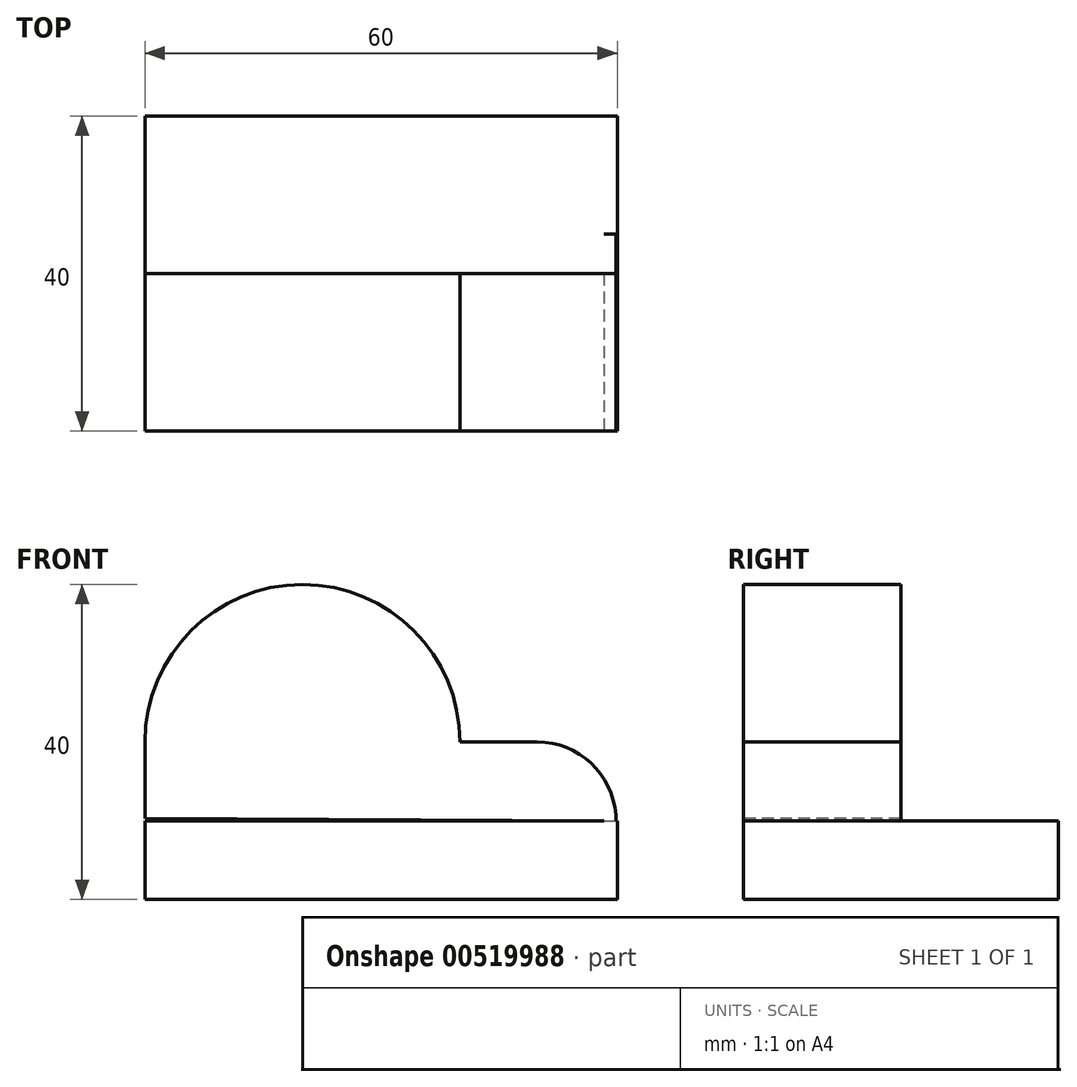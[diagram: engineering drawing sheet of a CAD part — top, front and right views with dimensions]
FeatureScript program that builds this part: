
annotation { "Feature Type Name" : "Feature", "Feature Type Description" : "" }
export const myFeature = defineFeature(function(context is Context, id is Id, definition is map)
    precondition{}
    {
        {
            var Q0;
            Q0=qCreatedBy(makeId("Top.planeOp"),FACE);
            var sketch = newSketch(context, id + "F0", { "sketchPlane" : qUnion([Q0])});
            skLineSegment(sketch, "E0.bottom", {"start": v(0, 0) * mm, "end": v(60, 0) * mm});
            skLineSegment(sketch, "E0.top", {"start": v(0, 40) * mm, "end": v(60, 40) * mm});
            skLineSegment(sketch, "E0.left", {"start": v(0, 0) * mm, "end": v(0, 40) * mm});
            skLineSegment(sketch, "E0.right", {"start": v(60, 0) * mm, "end": v(60, 40) * mm});
            skSolve(sketch);
        }
        {
            var Q0;
            Q0=makeQuery(id+"F0.imprint","IMPRINT",FACE,{"disambiguationData":[TD([[makeQuery(id+"F0.imprint","IMPRINT",EDGE,{"derivedFrom":sQuery(id+"F0.wireOp",EDGE,"E0.bottom")}),1.0]])]});
            extrude(context, id + "F1", {"entities" : qUnion([Q0]), "depth" : 10 * mm, "offsetDistance" : 25.4 * mm});
        }
        {
            var Q0;
            Q0=qCreatedBy(makeId("Front.planeOp"),FACE);
            var sketch = newSketch(context, id + "F2", { "sketchPlane" : qUnion([Q0])});
            skPoint(sketch, "E1", {"position": v(20, 20) * mm});
            skArc(sketch, "E2", {"start": v(40, 20) * mm, "mid": v(20, 40) * mm, "end": v(0, 20) * mm});
            skLineSegment(sketch, "E3", {"start": v(0, 20) * mm, "end": v(0, 10.31) * mm});
            skLineSegment(sketch, "E4", {"start": v(40, 20) * mm, "end": v(49.83, 20) * mm});
            skLineSegment(sketch, "E5", {"start": v(59.8, 10.72) * mm, "end": v(59.86, 10) * mm});
            skPoint(sketch, "E6.visualSharp", {"position": v(59.13, 20) * mm});
            skArc(sketch, "E6.filletArc", {"start": v(59.8, 10.72) * mm, "mid": v(56.64, 17.32) * mm, "end": v(49.83, 20) * mm});
            skLineSegment(sketch, "E7", {"start": v(0, 10.31) * mm, "end": v(59.86, 10) * mm});
            skSolve(sketch);
        }
        {
            var Q0;
            Q0=qCreatedBy(makeId("Front.planeOp"),FACE);
            var sketch = newSketch(context, id + "F3", { "sketchPlane" : qUnion([Q0])});
            skPoint(sketch, "E8", {"position": v(20, 20.2) * mm});
            skCircle(sketch, "E9", {"center": v(20, 20.2) * mm, "radius": 10 * mm});
            skSolve(sketch);
        }
        {
            var Q0;
            Q0 = qSketchRegion(id + "F3", true);
            var Q1;
            Q1=makeQuery(id+"F2.imprint","IMPRINT",FACE,{"disambiguationData":[TD([[makeQuery(id+"F2.imprint","IMPRINT",EDGE,{"derivedFrom":sQuery(id+"F2.wireOp",EDGE,"E2")}),1.0]])]});
            extrude(context, id + "F4", {"entities" : qUnion([Q0, Q1]), "operationType" : NewBodyOperationType.REMOVE, "oppositeDirection" : true, "depth" : 25 * mm, "offsetDistance" : 25.4 * mm});
        }
        {
            var Q0;
            Q0 = qSketchRegion(id + "F2", true);
            extrude(context, id + "F5", {"entities" : qUnion([Q0]), "operationType" : NewBodyOperationType.ADD, "oppositeDirection" : true, "depth" : 20 * mm, "offsetDistance" : 25.4 * mm});
        }
    });
